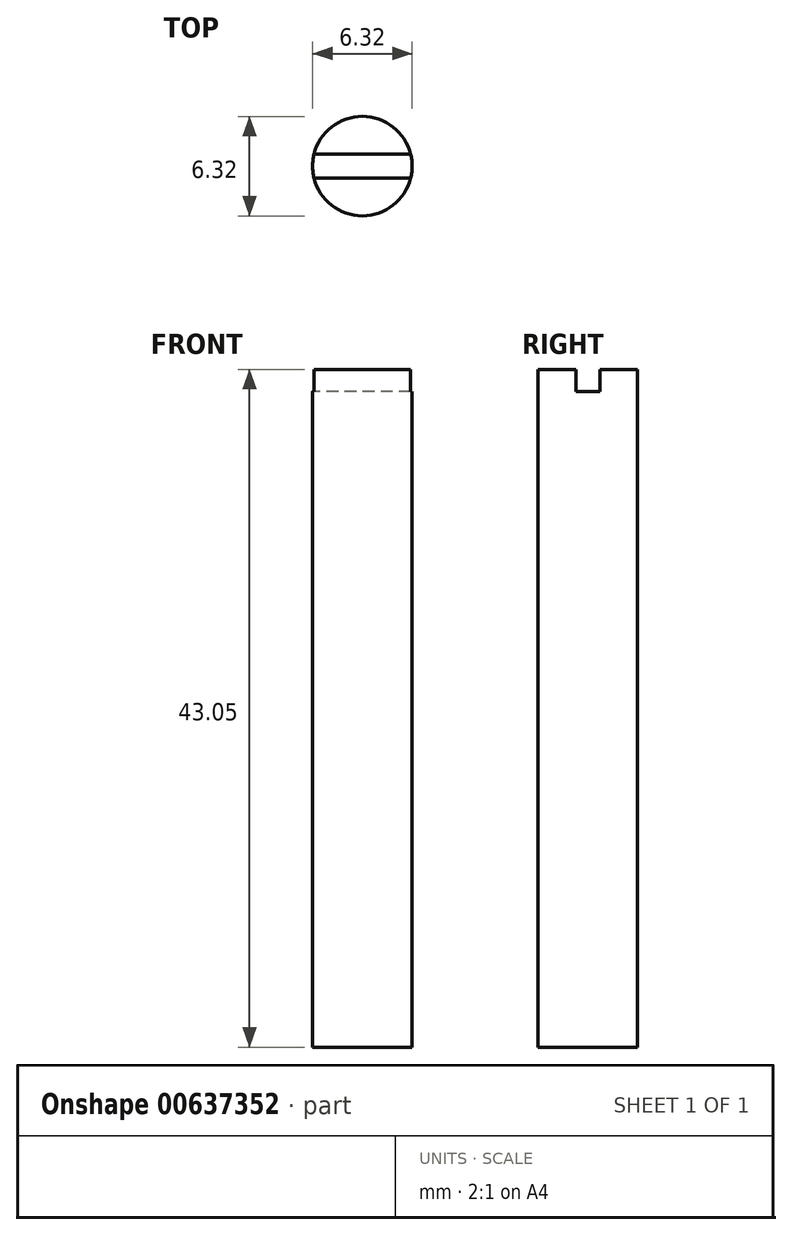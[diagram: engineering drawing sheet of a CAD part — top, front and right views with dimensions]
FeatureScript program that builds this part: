
annotation { "Feature Type Name" : "Feature", "Feature Type Description" : "" }
export const myFeature = defineFeature(function(context is Context, id is Id, definition is map)
    precondition{}
    {
        {
            var Q0;
            Q0=qCreatedBy(makeId("Top.planeOp"),FACE);
            var sketch = newSketch(context, id + "F0", { "sketchPlane" : qUnion([Q0])});
            skLineSegment(sketch, "E0", {"start": v(4.48, 0.76) * mm, "end": v(-4.48, 0.76) * mm});
            skLineSegment(sketch, "E1", {"start": v(4.48, -0.76) * mm, "end": v(-4.48, -0.76) * mm});
            skCircle(sketch, "E2", {"center": v(0, 0) * mm, "radius": 4.55 * mm});
            skCircle(sketch, "E3", {"center": v(0, 0) * mm, "radius": 3.16 * mm});
            skSolve(sketch);
        }
        {
            var Q0;
            {var subQ0=sQuery(id+"F0.wireOp",EDGE,"E2");var subQ1=sQuery(id+"F0.wireOp",EDGE,"E0");var subQ2=makeQuery(id+"F0.imprint","INTERSECT",VERTEX,{"disambiguationData":[OD(0.0)],"derivedFrom":[subQ1,subQ0]});Q0=makeQuery(id+"F0.imprint","IMPRINT",FACE,{"disambiguationData":[TD([[makeQuery(id+"F0.imprint","IMPRINT",EDGE,{"disambiguationData":[TD([[subQ2,-1.0]])],"derivedFrom":subQ1}),-1.0]])]});}
            var Q1;
            {var subQ0=sQuery(id+"F0.wireOp",EDGE,"E3");var subQ1=sQuery(id+"F0.wireOp",EDGE,"E0");var subQ2=makeQuery(id+"F0.imprint","INTERSECT",VERTEX,{"disambiguationData":[OD(0.0)],"derivedFrom":[subQ1,subQ0]});Q1=makeQuery(id+"F0.imprint","IMPRINT",FACE,{"disambiguationData":[TD([[makeQuery(id+"F0.imprint","IMPRINT",EDGE,{"disambiguationData":[TD([[subQ2,-1.0]])],"derivedFrom":subQ1}),-1.0]])]});}
            var Q2;
            {var subQ0=sQuery(id+"F0.wireOp",EDGE,"E3");var subQ1=sQuery(id+"F0.wireOp",EDGE,"E1");var subQ2=makeQuery(id+"F0.imprint","INTERSECT",VERTEX,{"disambiguationData":[OD(0.0)],"derivedFrom":[subQ1,subQ0]});Q2=makeQuery(id+"F0.imprint","IMPRINT",FACE,{"disambiguationData":[TD([[makeQuery(id+"F0.imprint","IMPRINT",EDGE,{"disambiguationData":[TD([[subQ2,-1.0]])],"derivedFrom":subQ1}),1.0]])]});}
            var Q3;
            {var subQ0=sQuery(id+"F0.wireOp",EDGE,"E2");var subQ1=sQuery(id+"F0.wireOp",EDGE,"E1");var subQ2=makeQuery(id+"F0.imprint","INTERSECT",VERTEX,{"disambiguationData":[OD(0.0)],"derivedFrom":[subQ1,subQ0]});Q3=makeQuery(id+"F0.imprint","IMPRINT",FACE,{"disambiguationData":[TD([[makeQuery(id+"F0.imprint","IMPRINT",EDGE,{"disambiguationData":[TD([[subQ2,-1.0]])],"derivedFrom":subQ1}),1.0]])]});}
            extrude(context, id + "F1", {"entities" : qUnion([Q0, Q1, Q2, Q3]), "depth" : 3.3 * mm, "offsetDistance" : 25.4 * mm});
        }
        {
            var Q0;
            {var subQ0=sQuery(id+"F0.wireOp",EDGE,"E3");var subQ1=sQuery(id+"F0.wireOp",EDGE,"E0");var subQ2=makeQuery(id+"F0.imprint","INTERSECT",VERTEX,{"disambiguationData":[OD(0.0)],"derivedFrom":[subQ1,subQ0]});Q0=makeQuery(id+"F0.imprint","IMPRINT",FACE,{"disambiguationData":[TD([[makeQuery(id+"F0.imprint","IMPRINT",EDGE,{"disambiguationData":[TD([[subQ2,-1.0]])],"derivedFrom":subQ1}),1.0]])]});}
            var Q1;
            {var subQ0=sQuery(id+"F0.wireOp",EDGE,"E2");var subQ1=sQuery(id+"F0.wireOp",EDGE,"E0");var subQ2=makeQuery(id+"F0.imprint","INTERSECT",VERTEX,{"disambiguationData":[OD(0.0)],"derivedFrom":[subQ1,subQ0]});Q1=makeQuery(id+"F0.imprint","IMPRINT",FACE,{"disambiguationData":[TD([[makeQuery(id+"F0.imprint","IMPRINT",EDGE,{"disambiguationData":[TD([[subQ2,-1.0]])],"derivedFrom":subQ1}),1.0]])]});}
            var Q2;
            {var subQ0=sQuery(id+"F0.wireOp",EDGE,"E2");var subQ1=sQuery(id+"F0.wireOp",EDGE,"E0");var subQ2=makeQuery(id+"F0.imprint","INTERSECT",VERTEX,{"disambiguationData":[OD(1.0)],"derivedFrom":[subQ1,subQ0]});Q2=makeQuery(id+"F0.imprint","IMPRINT",FACE,{"disambiguationData":[TD([[makeQuery(id+"F0.imprint","IMPRINT",EDGE,{"disambiguationData":[TD([[subQ2,1.0]])],"derivedFrom":subQ1}),1.0]])]});}
            extrude(context, id + "F2", {"entities" : qUnion([Q0, Q1, Q2]), "operationType" : NewBodyOperationType.ADD, "depth" : 1.9 * mm, "offsetDistance" : 25.4 * mm});
        }
        {
            var Q0;
            {var subQ0=sQuery(id+"F0.wireOp",EDGE,"E3");var subQ1=sQuery(id+"F0.wireOp",EDGE,"E0");var subQ2=makeQuery(id+"F0.imprint","INTERSECT",VERTEX,{"disambiguationData":[OD(0.0)],"derivedFrom":[subQ1,subQ0]});Q0=makeQuery(id+"F0.imprint","IMPRINT",FACE,{"disambiguationData":[TD([[makeQuery(id+"F0.imprint","IMPRINT",EDGE,{"disambiguationData":[TD([[subQ2,-1.0]])],"derivedFrom":subQ1}),-1.0]])]});}
            var Q1;
            {var subQ0=sQuery(id+"F0.wireOp",EDGE,"E3");var subQ1=sQuery(id+"F0.wireOp",EDGE,"E0");var subQ2=makeQuery(id+"F0.imprint","INTERSECT",VERTEX,{"disambiguationData":[OD(0.0)],"derivedFrom":[subQ1,subQ0]});Q1=makeQuery(id+"F0.imprint","IMPRINT",FACE,{"disambiguationData":[TD([[makeQuery(id+"F0.imprint","IMPRINT",EDGE,{"disambiguationData":[TD([[subQ2,-1.0]])],"derivedFrom":subQ1}),1.0]])]});}
            var Q2;
            {var subQ0=sQuery(id+"F0.wireOp",EDGE,"E3");var subQ1=sQuery(id+"F0.wireOp",EDGE,"E1");var subQ2=makeQuery(id+"F0.imprint","INTERSECT",VERTEX,{"disambiguationData":[OD(0.0)],"derivedFrom":[subQ1,subQ0]});Q2=makeQuery(id+"F0.imprint","IMPRINT",FACE,{"disambiguationData":[TD([[makeQuery(id+"F0.imprint","IMPRINT",EDGE,{"disambiguationData":[TD([[subQ2,-1.0]])],"derivedFrom":subQ1}),1.0]])]});}
            extrude(context, id + "F3", {"entities" : qUnion([Q0, Q1, Q2]), "operationType" : NewBodyOperationType.ADD, "oppositeDirection" : true, "depth" : 39.75 * mm, "offsetDistance" : 25.4 * mm});
        }
    });
